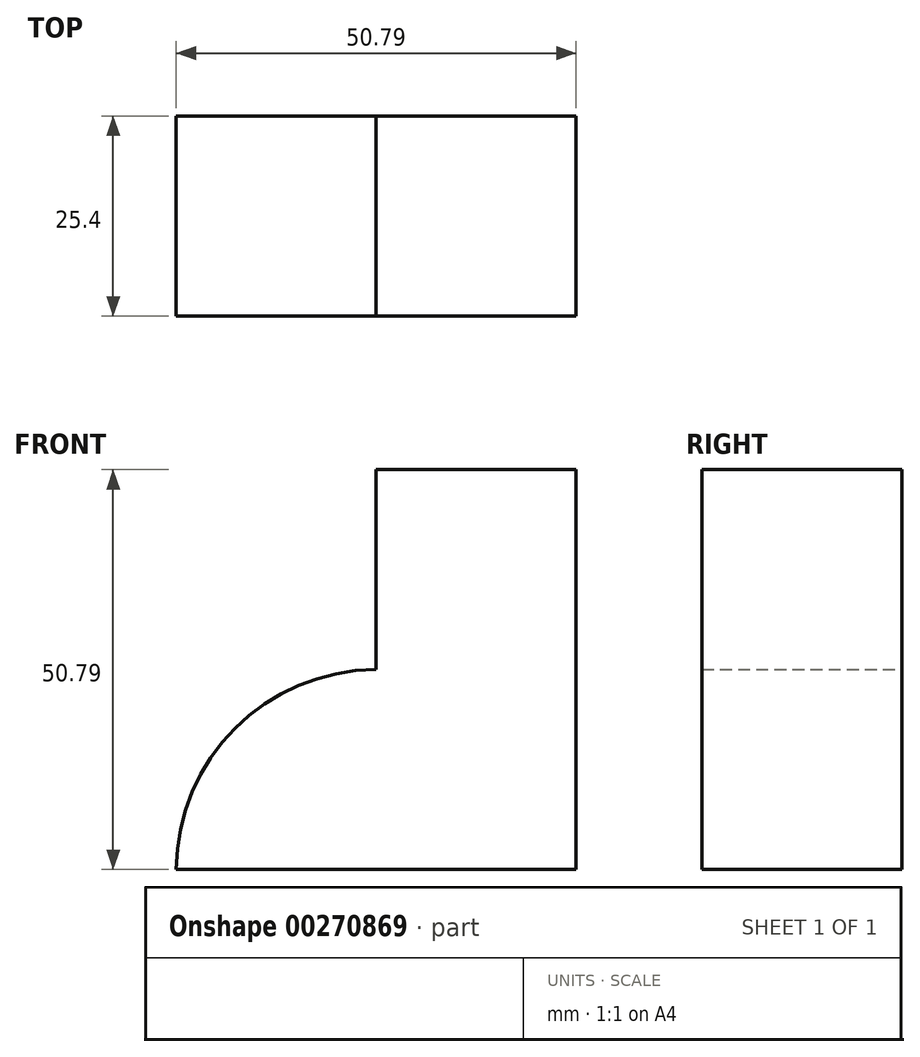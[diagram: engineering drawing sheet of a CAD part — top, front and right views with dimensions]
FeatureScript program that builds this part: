
annotation { "Feature Type Name" : "Feature", "Feature Type Description" : "" }
export const myFeature = defineFeature(function(context is Context, id is Id, definition is map)
    precondition{}
    {
        {
            var Q0;
            Q0=qCreatedBy(makeId("Front.planeOp"),FACE);
            var sketch = newSketch(context, id + "F0", { "sketchPlane" : qUnion([Q0])});
            skLineSegment(sketch, "E0", {"start": v(0, 0) * mm, "end": v(0, 50.8) * mm});
            skLineSegment(sketch, "E1", {"start": v(0, 0) * mm, "end": v(-50.8, 0) * mm});
            skLineSegment(sketch, "E2", {"start": v(0, 50.8) * mm, "end": v(-25.4, 50.8) * mm});
            skLineSegment(sketch, "E3", {"start": v(-25.4, 50.8) * mm, "end": v(-25.4, 25.4) * mm});
            skArc(sketch, "E4", {"start": v(-25.4, 25.4) * mm, "mid": v(-43.3, 17.91) * mm, "end": v(-50.8, 0) * mm});
            skSolve(sketch);
        }
        {
            var Q0;
            Q0 = qSketchRegion(id + "F0", true);
            extrude(context, id + "F1", {"entities" : qUnion([Q0]), "depth" : 25.4 * mm});
        }
    });
